# Revit family: 762902
name_source: partatom
category: Plumbing Fixtures
revit_build: Autodesk Revit 2015 (Build: 20140606_1530(x64)
units: mm (PartAtom-declared; Revit-internal decimal feet)

## types (1)
- Type 1
    Category = WC valve
    DLB090008 = Brass, Chrome plated
    Description = French manufacturer Delabie is a leader in the European sanitary ware market for non-domestic places. Water controls, solutions for disabled people, sanitary ware, for schools, leisure centres, offices, hospitals, airports…
    Diameter = 26 mm
    Features = Recessed time flow valve for direct flush: Multipurpose recessing housing. Chrome-plated metal wall plate Ø 195mm. Recessing depth can be adjusted 0 - 20mm. 3L/6L dual flush, can be adjusted to 2L/4L. Soft-touch operation. Vacuum breaker. Integrated stopcock and flow rate/flush volume adjuster. Solid brass body. Chrome-plated metal push-button. In-line inlet M¾". Outlet connection for PVC tube Ø 26/32mm. Acoustic level conforms with European standard EN 12541 class II.
    Finish = Chrome-plated
    Grade = BELGAQUA
    IntegralAccessoryOptions = Flush tube
    Manufacturer = DELABIE
    ManufacturerName = DELABIE
    Material = Solid brass
    Model = TEMPOFLUX 2
    Model number = 762902
    Name = 762902
    NominalHeight = Ø 19.5 cm
    NominalLength = Ø 19.5 cm
    Operation = Time flow valve for direct flush
    Polantis code = DLB090008
    ProductInformation = http://www.delabie.com
    SerialNumber = 3456330113908
    URL = http://www.delabie.com
    WarrantyDescription = Any manufacturing defect
    WarrantyDurationUnit = 10 years

## geometry (parser evidence)
native form markers: Sweep x3
no freeform markers — native parametric forms only
